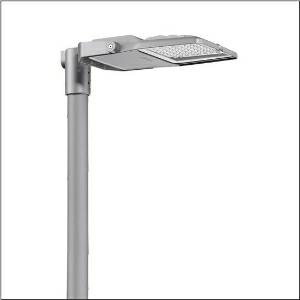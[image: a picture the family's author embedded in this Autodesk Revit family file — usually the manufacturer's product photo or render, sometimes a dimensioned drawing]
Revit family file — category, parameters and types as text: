
# Revit family: floodlight_fl_21_mini___pl43_5xa7776c2a3a_c8bd
name_source: partatom
category: Lighting Fixtures
units: mm (PartAtom-declared; Revit-internal decimal feet)

## family parameters
Cut with Voids When Loaded = No
Host = Face
Light Source = No
Part Type = Normal
Room Calculation Point = No
Round Connector Dimension = Use Diameter
Shared = No

## types (1)
- --- (1 x LED, 12500 lm, 89 W, 3000K)
    Apparent Load = 89 VA
    CIE Flux Codes = 27 78 99 100 100
    Color Rendering = 70
    Color Temperature = 3000K
    Default Elevation = 1800 mm
    Description = Floodlight FL 21 mini, floodlight, primary light control with lens, of PMMA, primary optical cover: protective disc, of toughened safety glass, transparent, light distribution: PL43, light emission: direct distribution, installation type: surface-mounted, LED, High Power LED, rated luminous flux: 12.500lm, luminous efficacy: 140lm/W, light colour: 730, colour temperature: 3000K, control gear: Smart Interface (Zhaga), control: flexible luminous flux parameterisation, time-dependent luminous flux control, constant luminous flux control, overheat protection, pre-setting: logarithmic dimming characteristic, with terminal, 6-pole, mains connection: 220..240V, AC, 50/60Hz, start of lifetime: 89W, end of service life: 94W, reduction: 43W, luminaire housing, of diecast aluminium, powder-coated, Siteco® metallic grey (DB 702S), corrosivity category C5 mid according to DIN EN ISO 12944, suitable for swimming pools, chlorine-resistant, sealing non-destructively replaceable, please order mast flange separately, mast bracket, of steel, galvanised, powder-coated, Siteco® metallic grey (DB 702S), Smart Interface below and above, protection rating (complete): IP66, insulation class (complete): insulation class II (safety insulation), certification: CE, ENEC, VDE, protection symbol: D, impact resistance: IK08, permissible operating ambient temperature: -40..+40°C, permissible operating ambient temperature for outdoor applications: -40..+50°C, standard: DIN EN 12944, LABS conformity tested according to VDMA 24364:2018-05, packaging unit: 1 piece

Light Distribution: PL43
    Height = 70 mm
    Lamp = 1 x LED
    Lamp Light Flux = 12500 lm
    Lamp Power = 89 W
    Lamp count = 1
    Length = 485 mm
    Luminous efficacy = 140 lm/W
    Manufacturer = Siteco
    ModVariant = No
    Model = 5XA7776C2A3A
    Number of Poles = 1
    OnlyDefault = Yes
    Power Factor = 1
    Product Name = Floodlight FL 21 mini | PL43
    Product group = floodlight | pylon annexe
    ProductGroupID = 6200
    Protection Class = Protection class II
    Protection Degree = IP 66
    RLX_Detail_Level = 1
    RLX_Emergency_Light_Flux = 0 lm
    RLX_Emergency_Type = 0
    RLX_Emergency_Type_DB = No
    RlxData = <blob elided: 100929 chars, md5=419ceac3>
    Socket = socket
    Standby Power = 0 W
    System Light Flux = 12500 lm
    System Power = 89 W
    Type Comments = factory setting: luminous flux: 100 % | dim-lin: 254 | 456 mA
    Type Image = l_1007125.jpg
    URL = http://relux.com
    VarID = @adj_161096
    Voltage = 0 V
    Weight = 0.00 kg
    Width = 337 mm

## geometry (parser evidence)
native form markers: Blend x4, Sweep x12
no freeform markers — native parametric forms only
